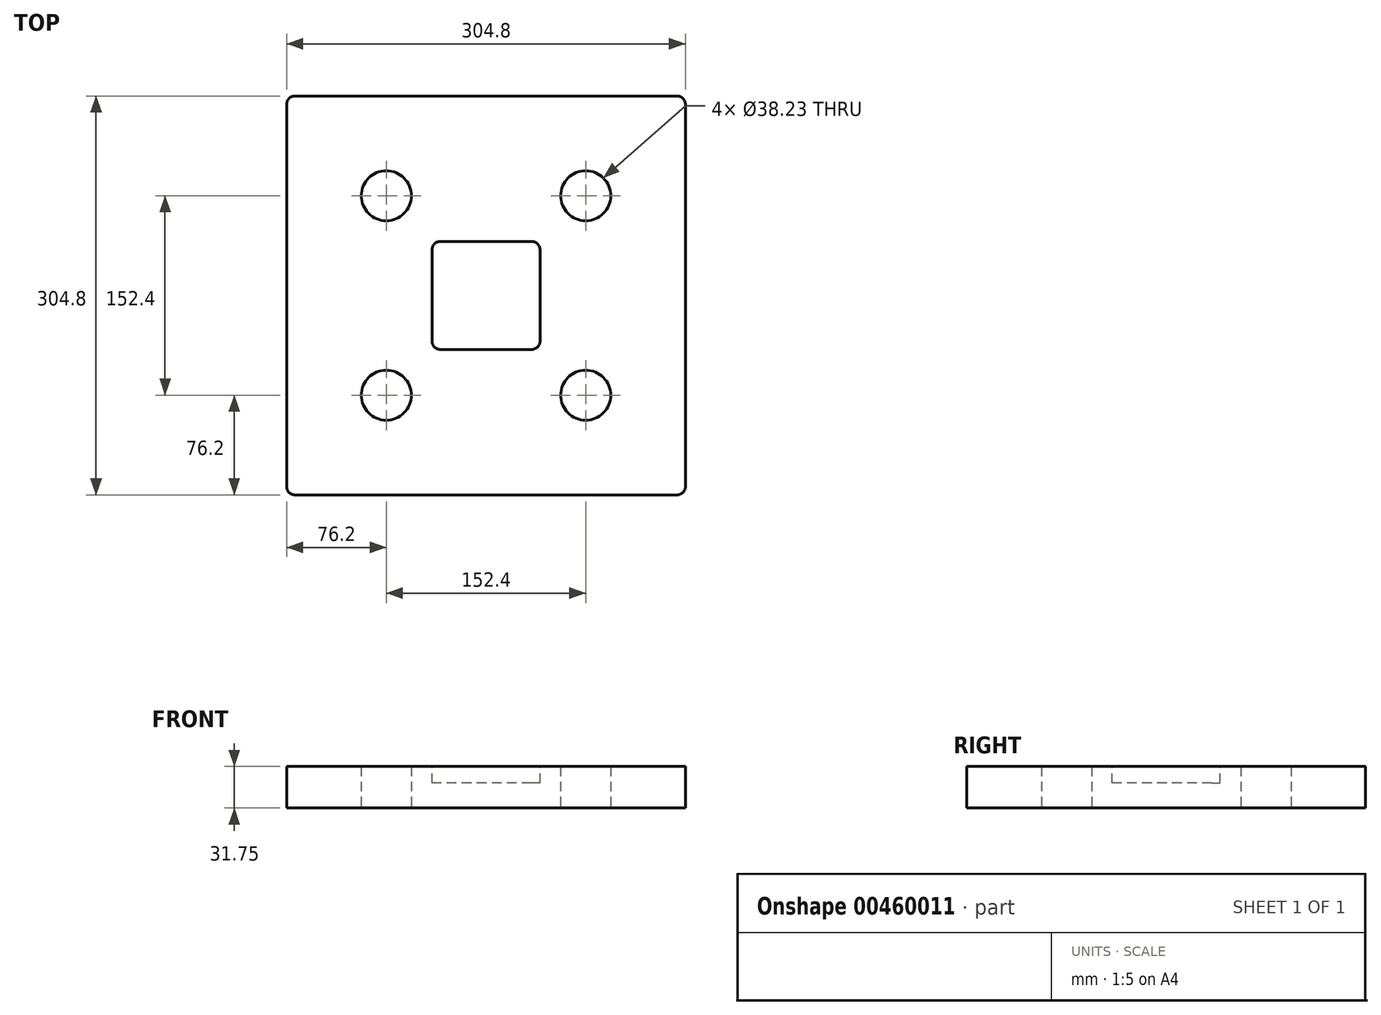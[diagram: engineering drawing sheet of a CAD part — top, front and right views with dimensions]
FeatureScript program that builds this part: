
annotation { "Feature Type Name" : "Feature", "Feature Type Description" : "" }
export const myFeature = defineFeature(function(context is Context, id is Id, definition is map)
    precondition{}
    {
        {
            var Q0;
            Q0=qCreatedBy(makeId("Top.planeOp"),FACE);
            var sketch = newSketch(context, id + "F0", { "sketchPlane" : qUnion([Q0])});
            skLineSegment(sketch, "E0.bottom", {"start": v(-152.4, -152.4) * mm, "end": v(152.4, -152.4) * mm});
            skLineSegment(sketch, "E0.top", {"start": v(-152.4, 152.4) * mm, "end": v(152.4, 152.4) * mm});
            skLineSegment(sketch, "E0.left", {"start": v(-152.4, -152.4) * mm, "end": v(-152.4, 152.4) * mm});
            skLineSegment(sketch, "E0.right", {"start": v(152.4, -152.4) * mm, "end": v(152.4, 152.4) * mm});
            skPoint(sketch, "E0.middle", {"position": v(0, 0) * mm});
            skCircle(sketch, "E1", {"center": v(76.2, 76.2) * mm, "radius": 19.11 * mm});
            skPoint(sketch, "E1.centerSnap0", {"position": v(76.2, 0) * mm});
            skPoint(sketch, "E1.centerSnap1", {"position": v(0, 76.2) * mm});
            skCircle(sketch, "E2.0.1.0", {"center": v(76.2, -76.2) * mm, "radius": 19.11 * mm});
            skCircle(sketch, "E2.1.0.0", {"center": v(-76.2, 76.2) * mm, "radius": 19.11 * mm});
            skCircle(sketch, "E2.1.1.0", {"center": v(-76.2, -76.2) * mm, "radius": 19.11 * mm});
            skLineSegment(sketch, "E2.direction1", {"start": v(76.2, 76.2) * mm, "end": v(-76.2, 76.2) * mm, "construction": true});
            skLineSegment(sketch, "E2.direction2", {"start": v(76.2, 76.2) * mm, "end": v(76.2, -76.2) * mm, "construction": true});
            skSolve(sketch);
        }
        {
            var Q0;
            Q0=makeQuery(id+"F0.imprint","IMPRINT",FACE,{"disambiguationData":[TD([[makeQuery(id+"F0.imprint","IMPRINT",EDGE,{"derivedFrom":sQuery(id+"F0.wireOp",EDGE,"E0.bottom")}),1.0]])]});
            extrude(context, id + "F1", {"entities" : qUnion([Q0]), "depth" : 31.75 * mm});
        }
        {
            var Q0;
            Q0=makeQuery(id+"F1.opExtrude","CAP_FACE",FACE,{"disambiguationData":[OSD([sQuery(id+"F0.wireOp",EDGE,"E0.bottom"),sQuery(id+"F0.wireOp",EDGE,"E0.top"),sQuery(id+"F0.wireOp",EDGE,"E0.left"),sQuery(id+"F0.wireOp",EDGE,"E0.right"),sQuery(id+"F0.wireOp",EDGE,"E1"),sQuery(id+"F0.wireOp",EDGE,"E2.0.1.0"),sQuery(id+"F0.wireOp",EDGE,"E2.1.0.0"),sQuery(id+"F0.wireOp",EDGE,"E2.1.1.0")])],"isStart":false});
            var sketch = newSketch(context, id + "F2", { "sketchPlane" : qUnion([Q0])});
            skLineSegment(sketch, "E3.bottom", {"start": v(34.93, 41.28) * mm, "end": v(-34.93, 41.28) * mm});
            skLineSegment(sketch, "E3.top", {"start": v(34.93, -41.28) * mm, "end": v(-34.93, -41.28) * mm});
            skLineSegment(sketch, "E3.left", {"start": v(41.28, 34.93) * mm, "end": v(41.28, -34.93) * mm});
            skLineSegment(sketch, "E3.right", {"start": v(-41.28, 34.93) * mm, "end": v(-41.28, -34.93) * mm});
            skPoint(sketch, "E3.middle", {"position": v(0, 0) * mm});
            skPoint(sketch, "E4.visualSharp", {"position": v(-41.28, 41.28) * mm});
            skArc(sketch, "E4.filletArc", {"start": v(-34.93, 41.28) * mm, "mid": v(-39.42, 39.42) * mm, "end": v(-41.28, 34.93) * mm});
            skPoint(sketch, "E5.visualSharp", {"position": v(41.28, 41.28) * mm});
            skArc(sketch, "E5.filletArc", {"start": v(41.28, 34.93) * mm, "mid": v(39.42, 39.42) * mm, "end": v(34.93, 41.28) * mm});
            skPoint(sketch, "E6.visualSharp", {"position": v(41.28, -41.28) * mm});
            skArc(sketch, "E6.filletArc", {"start": v(34.93, -41.28) * mm, "mid": v(39.42, -39.42) * mm, "end": v(41.28, -34.93) * mm});
            skPoint(sketch, "E7.visualSharp", {"position": v(-41.28, -41.28) * mm});
            skArc(sketch, "E7.filletArc", {"start": v(-41.28, -34.93) * mm, "mid": v(-39.42, -39.42) * mm, "end": v(-34.93, -41.28) * mm});
            skSolve(sketch);
        }
        {
            var Q0;
            Q0=makeQuery(id+"F2.imprint","IMPRINT",FACE,{"disambiguationData":[TD([[makeQuery(id+"F2.imprint","IMPRINT",EDGE,{"derivedFrom":sQuery(id+"F2.wireOp",EDGE,"E3.bottom")}),1.0]])]});
            extrude(context, id + "F3", {"entities" : qUnion([Q0]), "operationType" : NewBodyOperationType.REMOVE, "oppositeDirection" : true, "depth" : 12.7 * mm});
        }
        {
            var Q0;
            Q0=makeQuery(id+"F1.opExtrude","SWEPT_EDGE",EDGE,{"disambiguationData":[OSD([sQuery(id+"F0.wireOp",EDGE,"E0.top"),sQuery(id+"F0.wireOp",EDGE,"E0.right")])]});
            var Q1;
            Q1=makeQuery(id+"F1.opExtrude","SWEPT_EDGE",EDGE,{"disambiguationData":[OSD([sQuery(id+"F0.wireOp",EDGE,"E0.bottom"),sQuery(id+"F0.wireOp",EDGE,"E0.right")])]});
            var Q2;
            Q2=makeQuery(id+"F1.opExtrude","SWEPT_EDGE",EDGE,{"disambiguationData":[OSD([sQuery(id+"F0.wireOp",EDGE,"E0.top"),sQuery(id+"F0.wireOp",EDGE,"E0.left")])]});
            var Q3;
            Q3=makeQuery(id+"F1.opExtrude","SWEPT_EDGE",EDGE,{"disambiguationData":[OSD([sQuery(id+"F0.wireOp",EDGE,"E0.bottom"),sQuery(id+"F0.wireOp",EDGE,"E0.left")])]});
            fillet(context, id + "F4", {"entities" : qUnion([Q0, Q1, Q2, Q3]), "radius" : 6.35 * mm, "tangentPropagation" : true, "allowEdgeOverflow" : false});
        }
    });
